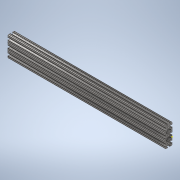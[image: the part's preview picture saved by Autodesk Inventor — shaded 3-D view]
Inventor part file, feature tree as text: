
AUTODESK INVENTOR PART (.ipt)
format: ipt  version: 2020 (Build 240168000, 168)  size: 385,024 bytes
history: native  units: in
note: dims shown in document units (in); Inventor stores cm internally (conversion verified against a paired STEP export)
features: sketch x2, extrude x1
ambient origin geometry x8: Origin, YZ Plane, XZ Plane, XY Plane, X Axis, Y Axis, Z Axis, Center Point
bodies: Solid1 (feature_tree)
feature tree (3):
  extrude  "Extrusion1"  [1 undecoded]
  sketch  "Sketch2"
  sketch  "Sketch1"  dims[d0=23.0in d1=0.0in]
note: 1 required parameter value undecoded (feature->parameter linkage not recoverable at this tier; creation-order binding heuristic only, values carry confidence <= 0.55)
